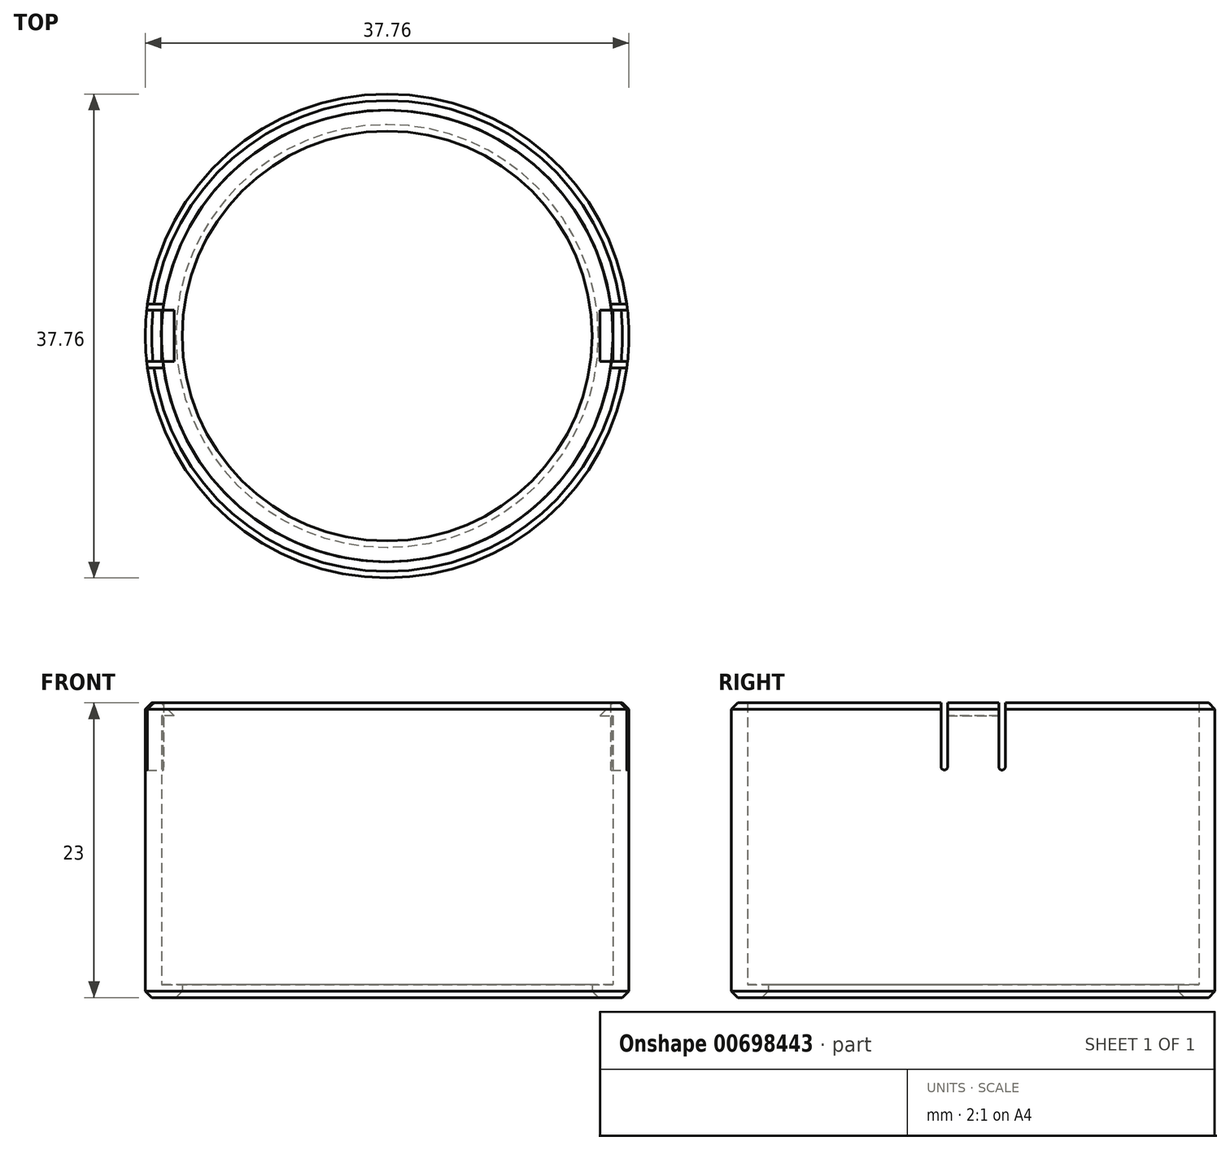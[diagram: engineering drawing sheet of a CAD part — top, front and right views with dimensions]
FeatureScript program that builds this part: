
annotation { "Feature Type Name" : "Feature", "Feature Type Description" : "" }
export const myFeature = defineFeature(function(context is Context, id is Id, definition is map)
    precondition{}
    {
        {
            var Q0;
            Q0=qCreatedBy(makeId("Top.planeOp"),FACE);
            var sketch = newSketch(context, id + "F0", { "sketchPlane" : qUnion([Q0])});
            skCircle(sketch, "E0", {"center": v(0, 0) * mm, "radius": 17.62 * mm});
            skCircle(sketch, "E1", {"center": v(0, 0) * mm, "radius": 18.88 * mm});
            skCircle(sketch, "E2", {"center": v(0, 0) * mm, "radius": 16 * mm});
            skSolve(sketch);
        }
        {
            var Q0;
            Q0=makeQuery(id+"F0.imprint","IMPRINT",FACE,{"disambiguationData":[TD([[makeQuery(id+"F0.imprint","IMPRINT",EDGE,{"derivedFrom":sQuery(id+"F0.wireOp",EDGE,"E0")}),-1.0]])]});
            extrude(context, id + "F1", {"entities" : qUnion([Q0]), "depth" : 23 * mm, "offsetDistance" : 25 * mm});
        }
        {
            var Q0;
            Q0=makeQuery(id+"F0.imprint","IMPRINT",FACE,{"disambiguationData":[TD([[makeQuery(id+"F0.imprint","IMPRINT",EDGE,{"derivedFrom":sQuery(id+"F0.wireOp",EDGE,"E0")}),1.0]])]});
            extrude(context, id + "F2", {"entities" : qUnion([Q0]), "operationType" : NewBodyOperationType.ADD, "depth" : 1 * mm, "offsetDistance" : 25 * mm});
        }
        {
            var Q0;
            Q0=makeQuery(id+"F1.opExtrude","CAP_EDGE",EDGE,{"disambiguationData":[OSD([sQuery(id+"F0.wireOp",EDGE,"E1")])],"isStart":true});
            var Q1;
            Q1=makeQuery(id+"F2.opExtrude","CAP_EDGE",EDGE,{"disambiguationData":[OSD([sQuery(id+"F0.wireOp",EDGE,"E2")])],"isStart":true});
            var Q2;
            Q2=makeQuery(id+"F1.opExtrude","CAP_EDGE",EDGE,{"disambiguationData":[OSD([sQuery(id+"F0.wireOp",EDGE,"E1")])],"isStart":false});
            chamfer(context, id + "F3", {"entities" : qUnion([Q0, Q1, Q2]), "width" : .5 * mm, "tangentPropagation" : true});
        }
        {
            var Q0;
            Q0=qCreatedBy(makeId("Right.planeOp"),FACE);
            var sketch = newSketch(context, id + "F4", { "sketchPlane" : qUnion([Q0])});
            skLineSegment(sketch, "E3", {"start": v(0, 0) * mm, "end": v(0, 23) * mm});
            skLineSegment(sketch, "E4", {"start": v(0, 23) * mm, "end": v(2, 23) * mm});
            skLineSegment(sketch, "E5", {"start": v(2, 23) * mm, "end": v(2, 18) * mm});
            skLineSegment(sketch, "E6", {"start": v(2, 18) * mm, "end": v(2.5, 18) * mm});
            skLineSegment(sketch, "E7", {"start": v(2.5, 18) * mm, "end": v(2.5, 23) * mm});
            skLineSegment(sketch, "E8", {"start": v(2.5, 23) * mm, "end": v(2, 23) * mm});
            skCircle(sketch, "E9", {"center": v(2.25, 18) * mm, "radius": 0.25 * mm});
            skLineSegment(sketch, "E10", {"start": v(0, 23) * mm, "end": v(0, 22.07) * mm});
            skLineSegment(sketch, "E11.MirrorCS", {"start": v(-2, 18) * mm, "end": v(-2.5, 18) * mm});
            skLineSegment(sketch, "E12.MirrorCS", {"start": v(-2.5, 18) * mm, "end": v(-2.5, 23) * mm});
            skLineSegment(sketch, "E13.MirrorCS", {"start": v(-2.5, 23) * mm, "end": v(-2, 23) * mm});
            skCircle(sketch, "E14.MirrorC", {"center": v(-2.25, 18) * mm, "radius": 0.25 * mm});
            skLineSegment(sketch, "E15.MirrorCS", {"start": v(-2, 23) * mm, "end": v(-2, 18) * mm});
            skSolve(sketch);
        }
        {
            var Q0;
            {var subQ0=sQuery(id+"F4.wireOp",EDGE,"E11.MirrorCS");Q0=makeQuery(id+"F4.imprint","IMPRINT",FACE,{"disambiguationData":[TD([[makeQuery(id+"F4.imprint","IMPRINT",EDGE,{"derivedFrom":subQ0}),-1.0]])]});}
            var Q1;
            {var subQ0=sQuery(id+"F4.wireOp",EDGE,"E11.MirrorCS");Q1=makeQuery(id+"F4.imprint","IMPRINT",FACE,{"disambiguationData":[TD([[makeQuery(id+"F4.imprint","IMPRINT",EDGE,{"derivedFrom":subQ0}),1.0]])]});}
            var Q2;
            {var subQ0=sQuery(id+"F4.wireOp",EDGE,"E12.MirrorCS");Q2=makeQuery(id+"F4.imprint","IMPRINT",FACE,{"disambiguationData":[TD([[makeQuery(id+"F4.imprint","IMPRINT",EDGE,{"derivedFrom":subQ0}),-1.0]])]});}
            var Q3;
            {var subQ0=sQuery(id+"F4.wireOp",EDGE,"E5");Q3=makeQuery(id+"F4.imprint","IMPRINT",FACE,{"disambiguationData":[TD([[makeQuery(id+"F4.imprint","IMPRINT",EDGE,{"derivedFrom":subQ0}),1.0]])]});}
            var Q4;
            {var subQ0=sQuery(id+"F4.wireOp",EDGE,"E6");Q4=makeQuery(id+"F4.imprint","IMPRINT",FACE,{"disambiguationData":[TD([[makeQuery(id+"F4.imprint","IMPRINT",EDGE,{"derivedFrom":subQ0}),1.0]])]});}
            var Q5;
            {var subQ0=sQuery(id+"F4.wireOp",EDGE,"E6");Q5=makeQuery(id+"F4.imprint","IMPRINT",FACE,{"disambiguationData":[TD([[makeQuery(id+"F4.imprint","IMPRINT",EDGE,{"derivedFrom":subQ0}),-1.0]])]});}
            extrude(context, id + "F5", {"entities" : qUnion([Q0, Q1, Q2, Q3, Q4, Q5]), "operationType" : NewBodyOperationType.REMOVE, "oppositeDirection" : true, "depth" : 25 * mm, "offsetDistance" : 25 * mm, "hasSecondDirection" : true, "secondDirectionOppositeDirection" : false, "secondDirectionDepth" : 25 * mm});
        }
        {
            var Q0;
            {var subQ0=sQuery(id+"F0.wireOp",EDGE,"E0");var subQ1=sQuery(id+"F0.wireOp",EDGE,"E1");Q0=makeQuery(id+"F5.boolean.opBoolean","SPLIT",FACE,{"disambiguationData":[TD([makeQuery(id+"F1.opExtrude","SWEPT_FACE",FACE,{"disambiguationData":[OSD([subQ0])]}),makeQuery(id+"F1.opExtrude","SWEPT_FACE",FACE,{"disambiguationData":[OSD([subQ1])]}),makeQuery(id+"F5.opExtrude","SWEPT_FACE",FACE,{"disambiguationData":[OSD([sQuery(id+"F4.wireOp",EDGE,"E5")])]}),makeQuery(id+"F5.opExtrude","SWEPT_FACE",FACE,{"disambiguationData":[OSD([sQuery(id+"F4.wireOp",EDGE,"E15.MirrorCS")])]})]),OD(0.0)],"derivedFrom":makeQuery(id+"F1.opExtrude","CAP_FACE",FACE,{"disambiguationData":[OSD([subQ0,subQ1])],"isStart":false})});}
            var sketch = newSketch(context, id + "F6", { "sketchPlane" : qUnion([Q0])});
            skLineSegment(sketch, "E16", {"start": v(-17.62, 0) * mm, "end": v(-16.62, 0) * mm});
            skLineSegment(sketch, "E17", {"start": v(-16.62, 0) * mm, "end": v(-16.62, 2) * mm});
            skLineSegment(sketch, "E18", {"start": v(-16.62, 2) * mm, "end": v(-17.51, 2) * mm});
            skLineSegment(sketch, "E19", {"start": v(-17.51, 2) * mm, "end": v(-17.89, 2) * mm});
            skLineSegment(sketch, "E20", {"start": v(-17.89, 2) * mm, "end": v(-17.89, -2) * mm});
            skLineSegment(sketch, "E21", {"start": v(-17.89, -2) * mm, "end": v(-16.62, -2) * mm});
            skLineSegment(sketch, "E22", {"start": v(-16.62, -2) * mm, "end": v(-16.62, 0) * mm});
            skLineSegment(sketch, "E23", {"start": v(0, 0) * mm, "end": v(0, 5.95) * mm});
            skLineSegment(sketch, "E24.MirrorCS", {"start": v(17.51, 2) * mm, "end": v(17.89, 2) * mm});
            skLineSegment(sketch, "E25.MirrorCS", {"start": v(17.62, 0) * mm, "end": v(16.62, 0) * mm});
            skLineSegment(sketch, "E26.MirrorCS", {"start": v(17.89, -2) * mm, "end": v(16.62, -2) * mm});
            skLineSegment(sketch, "E27.MirrorCS", {"start": v(16.62, -2) * mm, "end": v(16.62, 0) * mm});
            skLineSegment(sketch, "E28.MirrorCS", {"start": v(16.62, 2) * mm, "end": v(17.51, 2) * mm});
            skLineSegment(sketch, "E29.MirrorCS", {"start": v(17.89, 2) * mm, "end": v(17.89, -2) * mm});
            skLineSegment(sketch, "E30.MirrorCS", {"start": v(16.62, 0) * mm, "end": v(16.62, 2) * mm});
            skSolve(sketch);
        }
        {
            var Q0;
            {var subQ0=sQuery(id+"F6.wireOp",EDGE,"E16");Q0=makeQuery(id+"F6.imprint","IMPRINT",FACE,{"disambiguationData":[TD([[makeQuery(id+"F6.imprint","IMPRINT",EDGE,{"derivedFrom":subQ0}),1.0]])]});}
            var Q1;
            {var subQ0=sQuery(id+"F6.wireOp",EDGE,"E16");Q1=makeQuery(id+"F6.imprint","IMPRINT",FACE,{"disambiguationData":[TD([[makeQuery(id+"F6.imprint","IMPRINT",EDGE,{"derivedFrom":subQ0}),-1.0]])]});}
            var Q2;
            Q2=makeQuery(id+"F6.imprint","IMPRINT",FACE,{"disambiguationData":[TD([[makeQuery(id+"F6.imprint","IMPRINT",EDGE,{"derivedFrom":sQuery(id+"F6.wireOp",EDGE,"E24.MirrorCS")}),-1.0]])]});
            extrude(context, id + "F7", {"entities" : qUnion([Q0, Q1, Q2]), "operationType" : NewBodyOperationType.ADD, "oppositeDirection" : true, "depth" : 1 * mm, "offsetDistance" : 25 * mm});
        }
        {
            var Q0;
            Q0=makeQuery(id+"F7.opExtrude","CAP_EDGE",EDGE,{"disambiguationData":[OSD([sQuery(id+"F6.wireOp",EDGE,"E17"),sQuery(id+"F6.wireOp",EDGE,"E22")])],"isStart":true});
            var Q1;
            Q1=makeQuery(id+"F7.opExtrude","CAP_EDGE",EDGE,{"disambiguationData":[OSD([sQuery(id+"F6.wireOp",EDGE,"E27.MirrorCS"),sQuery(id+"F6.wireOp",EDGE,"E30.MirrorCS")])],"isStart":true});
            chamfer(context, id + "F8", {"entities" : qUnion([Q0, Q1]), "width" : 1 * mm, "tangentPropagation" : true});
        }
    });
